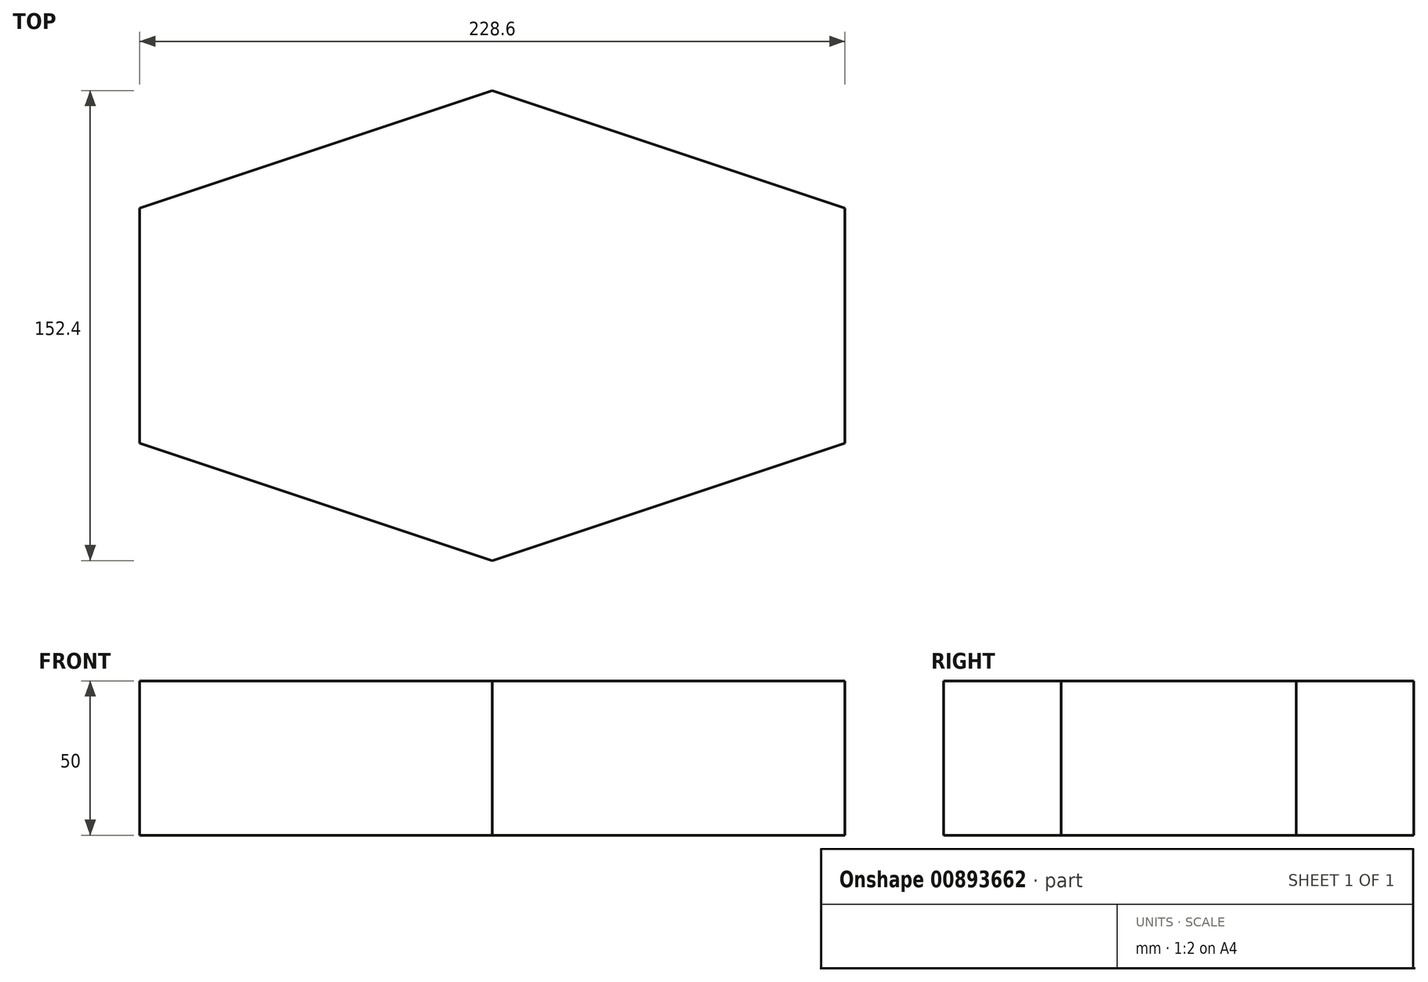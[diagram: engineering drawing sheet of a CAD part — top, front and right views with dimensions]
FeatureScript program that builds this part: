
annotation { "Feature Type Name" : "Feature", "Feature Type Description" : "" }
export const myFeature = defineFeature(function(context is Context, id is Id, definition is map)
    precondition{}
    {
        {
            var Q0;
            Q0=qCreatedBy(makeId("Top.planeOp"),FACE);
            var sketch = newSketch(context, id + "F0", { "sketchPlane" : qUnion([Q0])});
            skLineSegment(sketch, "E0", {"start": v(-114.3, 38.1) * mm, "end": v(-114.3, -38.1) * mm});
            skLineSegment(sketch, "E1", {"start": v(-114.3, 38.1) * mm, "end": v(0, 76.2) * mm});
            skLineSegment(sketch, "E2", {"start": v(0, 76.2) * mm, "end": v(114.3, 38.1) * mm});
            skLineSegment(sketch, "E3", {"start": v(114.3, 38.1) * mm, "end": v(114.3, -38.1) * mm});
            skLineSegment(sketch, "E4", {"start": v(114.3, -38.1) * mm, "end": v(0, -76.2) * mm});
            skLineSegment(sketch, "E5", {"start": v(-114.3, -38.1) * mm, "end": v(0, -76.2) * mm});
            skPoint(sketch, "E6.end.orphan", {"position": v(114.3, 0) * mm});
            skSolve(sketch);
        }
        {
            var Q0;
            Q0 = qSketchRegion(id + "F0", true);
            extrude(context, id + "F1", {"entities" : qUnion([Q0]), "depth" : 50 * mm, "offsetDistance" : 25.4 * mm});
        }
    });
